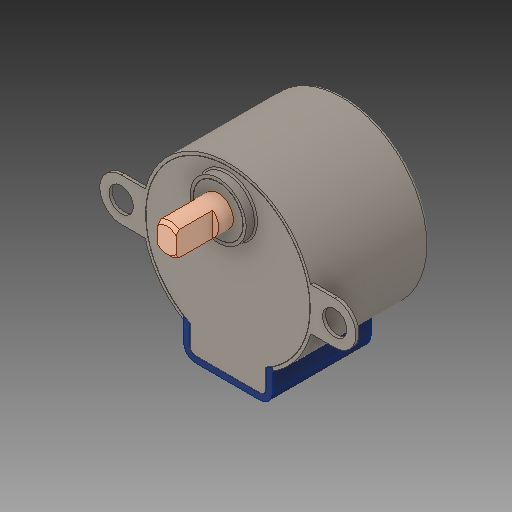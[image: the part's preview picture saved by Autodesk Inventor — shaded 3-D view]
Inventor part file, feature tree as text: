
AUTODESK INVENTOR PART (.ipt)
format: ipt  version: 2019 (Build 230136000, 136)  size: 645,632 bytes
history: mixed  units: mm
features: other x30, fillet x1, chamfer x1, imported_body x1
ambient origin geometry x8: Origin, YZ Plane, XZ Plane, XY Plane, X Axis, Y Axis, Z Axis, Center Point
bodies: Body1 (imported_parasolid), Body2 (imported_parasolid), Body3 (imported_parasolid), Body4 (imported_parasolid), Body5 (imported_parasolid), Body6 (imported_parasolid), Body7 (imported_parasolid), Body8 (imported_parasolid), Body9 (imported_parasolid), Body10 (imported_parasolid), Body11 (imported_parasolid), Body12 (imported_parasolid), Body13 (imported_parasolid), Body14 (imported_parasolid), Body15 (imported_parasolid), Body16 (imported_parasolid)
feature tree (33):
  other  "Твердое тело1"
  other  "Твердое тело2"
  other  "Твердое тело3"
  other  "Твердое тело4"
  other  "Твердое тело5"
  other  "Твердое тело6"
  other  "Твердое тело7"
  other  "Твердое тело8"
  other  "Твердое тело9"
  other  "Твердое тело10"
  other  "Твердое тело11"
  other  "Твердое тело12"
  other  "Твердое тело13"
  other  "Твердое тело14"
  other  "Твердое тело15"
  other  "Твердое тело16"
  fillet  "Redondeo3"  [1 undecoded]
  other  "Cortar-Extruir5"
  other  "Saliente-Extruir7[1]"
  other  "Saliente-Extruir7[2]"
  other  "Saliente-Extruir7[3]"
  other  "Saliente-Extruir7[4]"
  other  "Saliente-Extruir7[5]"
  other  "Saliente-Extruir7[6]"
  other  "Saliente-Extruir7[7]"
  other  "Saliente-Extruir7[8]"
  other  "Saliente-Extruir7[9]"
  other  "Saliente-Extruir7[10]"
  other  "Saliente-Extruir7[11]"
  other  "Saliente-Extruir7[12]"
  other  "Saliente-Extruir7[13]"
  chamfer  "Chaflán1"  [1 undecoded]
  imported_body  NMx_Import_Brep_tag  [imported B-rep: ~19 faces, bbox_mm=None]
note: 2 required parameter values undecoded (feature->parameter linkage not recoverable at this tier; creation-order binding heuristic only, values carry confidence <= 0.55)
